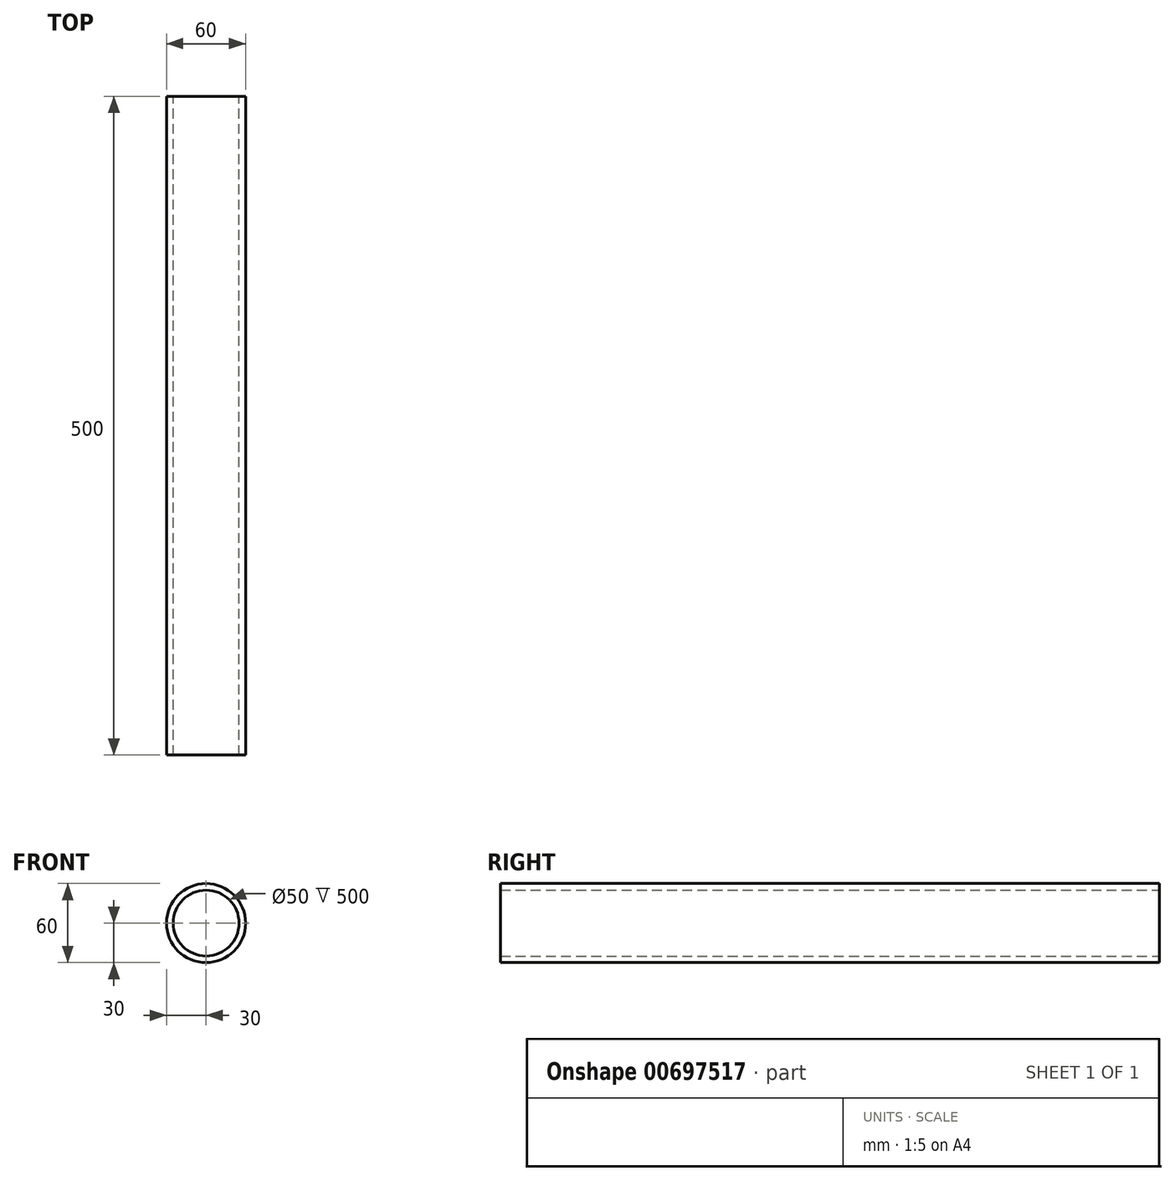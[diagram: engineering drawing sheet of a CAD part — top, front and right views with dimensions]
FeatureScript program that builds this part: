
annotation { "Feature Type Name" : "Feature", "Feature Type Description" : "" }
export const myFeature = defineFeature(function(context is Context, id is Id, definition is map)
    precondition{}
    {
        {
            var Q0;
            Q0=qCreatedBy(makeId("Front.planeOp"),FACE);
            var sketch = newSketch(context, id + "F0", { "sketchPlane" : qUnion([Q0])});
            skCircle(sketch, "E0", {"center": v(0, 0) * mm, "radius": 30 * mm});
            skCircle(sketch, "E1", {"center": v(0, 0) * mm, "radius": 25 * mm});
            skSolve(sketch);
        }
        {
            var Q0;
            Q0=makeQuery(id+"F0.imprint","IMPRINT",FACE,{"disambiguationData":[TD([[makeQuery(id+"F0.imprint","IMPRINT",EDGE,{"derivedFrom":sQuery(id+"F0.wireOp",EDGE,"E0")}),1.0]])]});
            extrude(context, id + "F1", {"entities" : qUnion([Q0]), "endBound" : BoundingType.SYMMETRIC, "depth" : 500 * mm, "offsetDistance" : 25 * mm});
        }
    });
